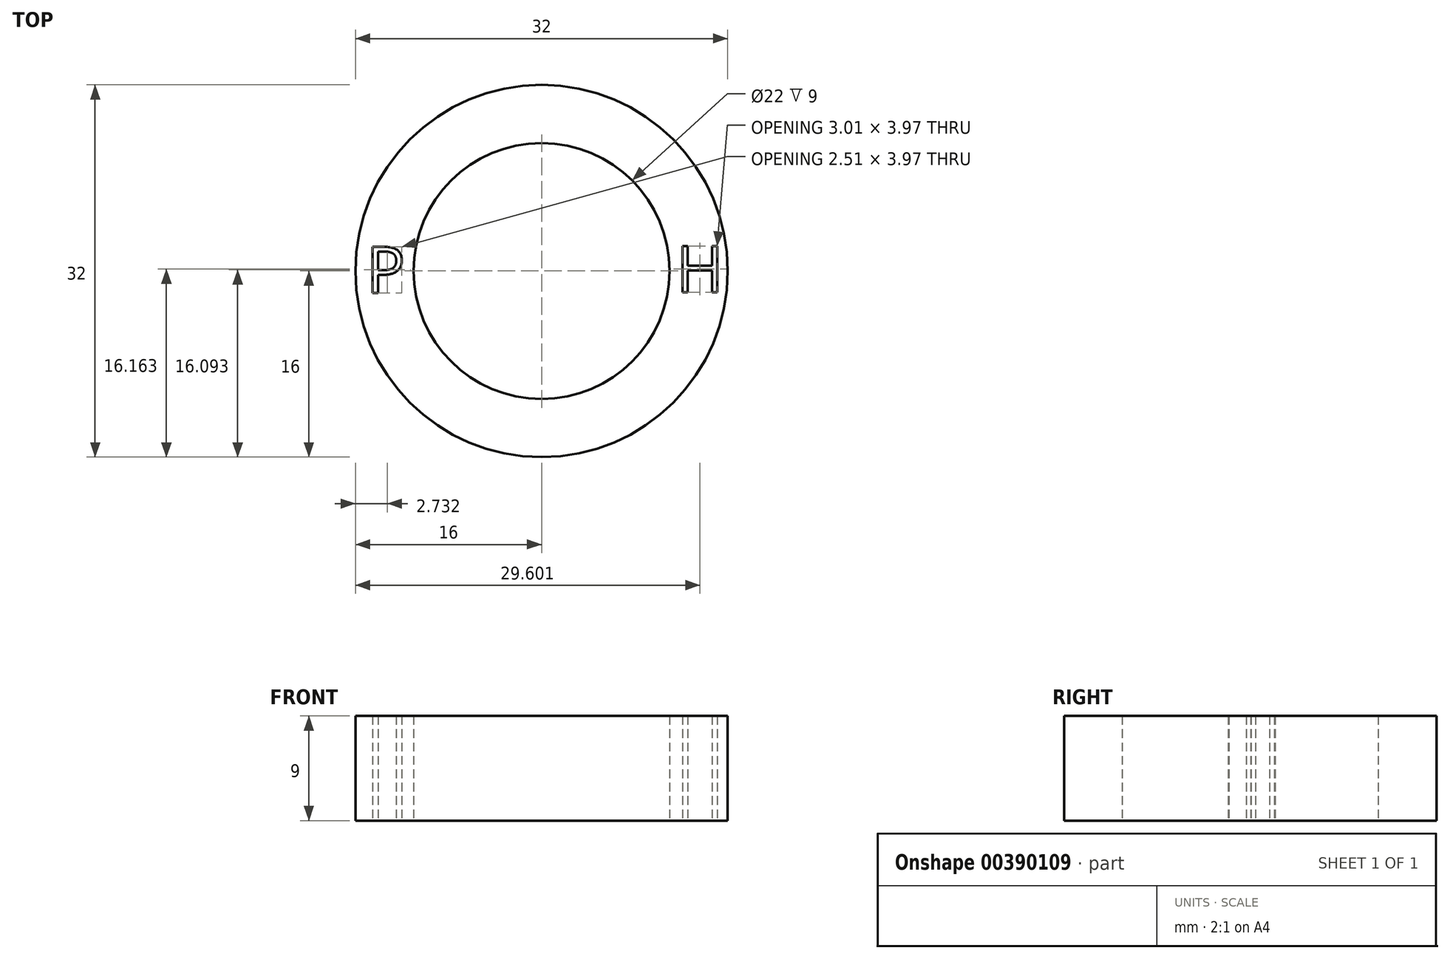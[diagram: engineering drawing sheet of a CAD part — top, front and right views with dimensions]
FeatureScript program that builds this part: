
annotation { "Feature Type Name" : "Feature", "Feature Type Description" : "" }
export const myFeature = defineFeature(function(context is Context, id is Id, definition is map)
    precondition{}
    {
        {
            var Q0;
            Q0=qCreatedBy(makeId("Top.planeOp"),FACE);
            var sketch = newSketch(context, id + "F0", { "sketchPlane" : qUnion([Q0])});
            skCircle(sketch, "E0", {"center": v(0, 0) * mm, "radius": 16 * mm});
            skSolve(sketch);
        }
        {
            var Q0;
            Q0=qCreatedBy(makeId("Top.planeOp"),FACE);
            var sketch = newSketch(context, id + "F1", { "sketchPlane" : qUnion([Q0])});
            skCircle(sketch, "E1", {"center": v(0, 0) * mm, "radius": 11 * mm});
            skSolve(sketch);
        }
        {
            var Q0;
            Q0=makeQuery(id+"F0.imprint","IMPRINT",FACE,{"disambiguationData":[TD([[makeQuery(id+"F0.imprint","IMPRINT",EDGE,{"derivedFrom":sQuery(id+"F0.wireOp",EDGE,"E0")}),1.0]])]});
            extrude(context, id + "F2", {"entities" : qUnion([Q0]), "depth" : 9 * mm});
        }
        {
            var Q0;
            Q0=makeQuery(id+"F1.imprint","IMPRINT",FACE,{"disambiguationData":[TD([[makeQuery(id+"F1.imprint","IMPRINT",EDGE,{"derivedFrom":sQuery(id+"F1.wireOp",EDGE,"E1")}),1.0]])]});
            extrude(context, id + "F3", {"entities" : qUnion([Q0]), "operationType" : NewBodyOperationType.REMOVE, "depth" : 74.17 * mm});
        }
        {
            var Q0;
            Q0=qCreatedBy(makeId("Top.planeOp"),FACE);
            var sketch = newSketch(context, id + "F4", { "sketchPlane" : qUnion([Q0])});
            skText(sketch, "E2", { "text": "P\n", "fontName": "OpenSans-Regular.ttf"});
            const initialGuessF4  = {"E2": [-0.01507, -0.00189, 1, 0, 0.004]};
            skSetInitialGuess(sketch, initialGuessF4);
            skSolve(sketch);
        }
        {
            var Q0;
            Q0 = qSketchRegion(id + "F4", true);
            extrude(context, id + "F5", {"entities" : qUnion([Q0]), "operationType" : NewBodyOperationType.REMOVE, "depth" : 50 * mm, "offsetDistance" : 25 * mm});
        }
        {
            var Q0;
            Q0=qCreatedBy(makeId("Top.planeOp"),FACE);
            var sketch = newSketch(context, id + "F6", { "sketchPlane" : qUnion([Q0])});
            skText(sketch, "E3", { "text": "H", "fontName": "OpenSans-Regular.ttf"});
            const initialGuessF6  = {"E3": [0.01155, -0.00182, 1, 0, 0.004]};
            skSetInitialGuess(sketch, initialGuessF6);
            skSolve(sketch);
        }
        {
            var Q0;
            Q0 = qSketchRegion(id + "F6", true);
            extrude(context, id + "F7", {"entities" : qUnion([Q0]), "operationType" : NewBodyOperationType.REMOVE, "depth" : 25 * mm, "offsetDistance" : 25 * mm});
        }
    });
